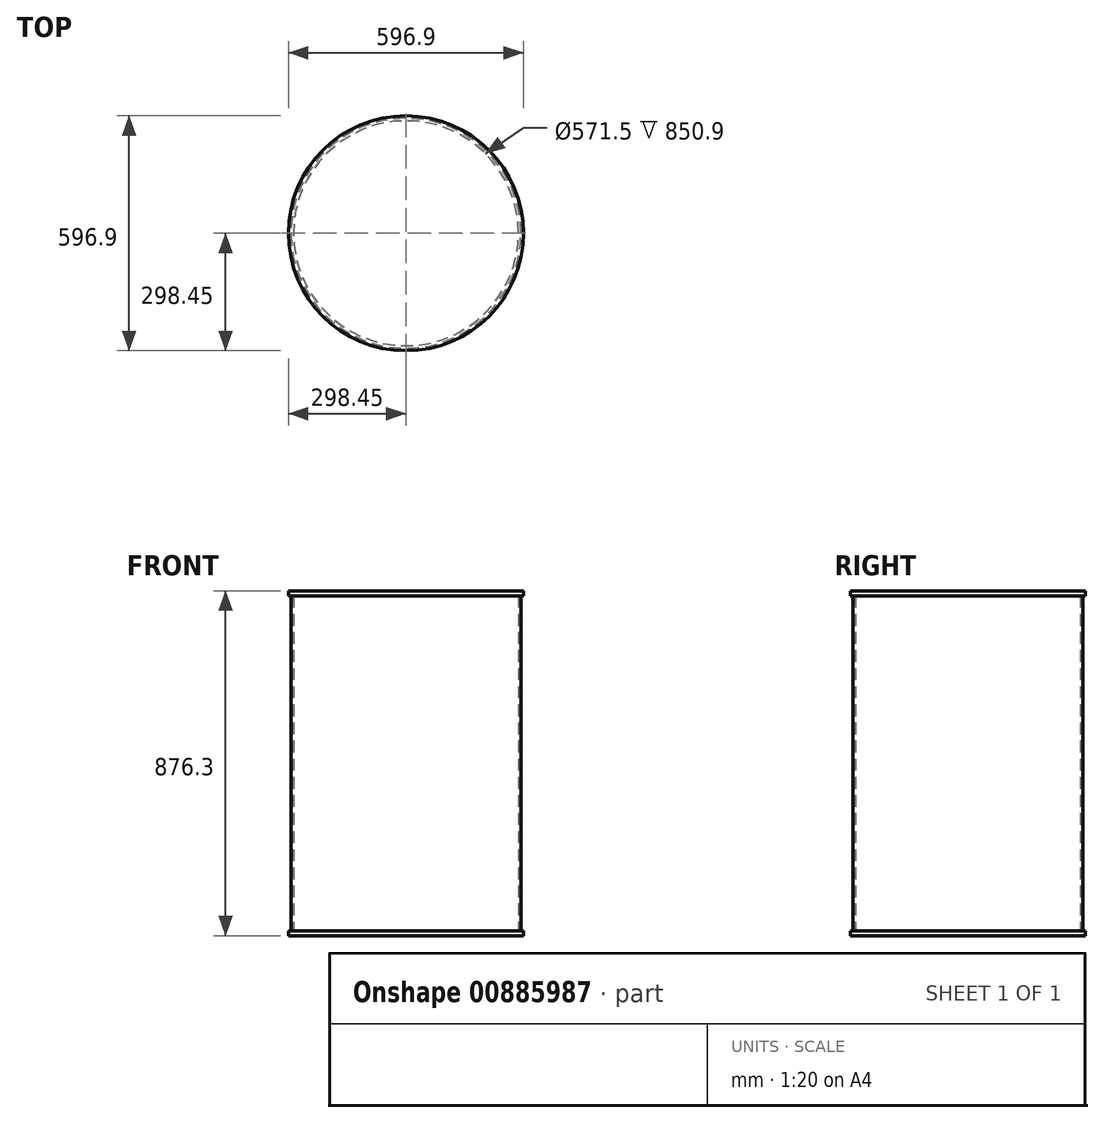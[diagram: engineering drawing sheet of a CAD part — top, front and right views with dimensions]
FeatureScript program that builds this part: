
annotation { "Feature Type Name" : "Feature", "Feature Type Description" : "" }
export const myFeature = defineFeature(function(context is Context, id is Id, definition is map)
    precondition{}
    {
        {
            var Q0;
            Q0=qCreatedBy(makeId("Top.planeOp"),FACE);
            var sketch = newSketch(context, id + "F0", { "sketchPlane" : qUnion([Q0])});
            skCircle(sketch, "E0", {"center": v(0, 0) * mm, "radius": 298.45 * mm});
            skCircle(sketch, "E1", {"center": v(0, 0) * mm, "radius": 292.1 * mm});
            skCircle(sketch, "E2", {"center": v(0, 0) * mm, "radius": 285.75 * mm});
            skSolve(sketch);
        }
        {
            var Q0;
            Q0=makeQuery(id+"F0.imprint","IMPRINT",FACE,{"disambiguationData":[TD([[makeQuery(id+"F0.imprint","IMPRINT",EDGE,{"derivedFrom":sQuery(id+"F0.wireOp",EDGE,"E0")}),1.0]])]});
            var Q1;
            Q1=makeQuery(id+"F0.imprint","IMPRINT",FACE,{"disambiguationData":[TD([[makeQuery(id+"F0.imprint","IMPRINT",EDGE,{"derivedFrom":sQuery(id+"F0.wireOp",EDGE,"E1")}),1.0]])]});
            var Q2;
            Q2=makeQuery(id+"F0.imprint","IMPRINT",FACE,{"disambiguationData":[TD([[makeQuery(id+"F0.imprint","IMPRINT",EDGE,{"derivedFrom":sQuery(id+"F0.wireOp",EDGE,"E2")}),1.0]])]});
            extrude(context, id + "F1", {"entities" : qUnion([Q0, Q1, Q2]), "depth" : 12.7 * mm, "offsetDistance" : 25.4 * mm});
        }
        {
            var Q0;
            Q0=makeQuery(id+"F0.imprint","IMPRINT",FACE,{"disambiguationData":[TD([[makeQuery(id+"F0.imprint","IMPRINT",EDGE,{"derivedFrom":sQuery(id+"F0.wireOp",EDGE,"E1")}),1.0]])]});
            extrude(context, id + "F2", {"entities" : qUnion([Q0]), "operationType" : NewBodyOperationType.ADD, "depth" : 876.3 * mm, "offsetDistance" : 25.4 * mm});
        }
        {
            var Q0;
            Q0=makeQuery(id+"F2.opExtrude","CAP_FACE",FACE,{"disambiguationData":[OSD([sQuery(id+"F0.wireOp",EDGE,"E1"),sQuery(id+"F0.wireOp",EDGE,"E2")])],"isStart":false});
            var sketch = newSketch(context, id + "F3", { "sketchPlane" : qUnion([Q0])});
            skCircle(sketch, "E3", {"center": v(0, 0) * mm, "radius": 298.45 * mm});
            skSolve(sketch);
        }
        {
            var Q0;
            Q0 = qSketchRegion(id + "F3", true);
            extrude(context, id + "F4", {"entities" : qUnion([Q0]), "operationType" : NewBodyOperationType.ADD, "oppositeDirection" : true, "depth" : 12.7 * mm, "offsetDistance" : 25.4 * mm});
        }
    });
